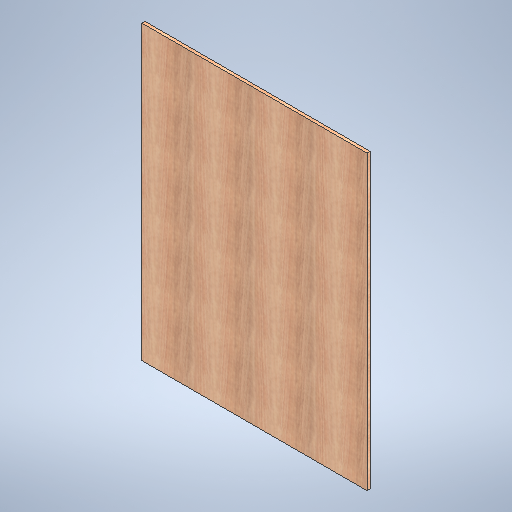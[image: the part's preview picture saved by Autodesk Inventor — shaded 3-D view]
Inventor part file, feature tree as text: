
AUTODESK INVENTOR PART (.ipt)
format: ipt  version: 2025 (Build 290162010, 162A)  size: 392,192 bytes
history: native  units: in
note: dims shown in document units (in); Inventor stores cm internally (conversion verified against a paired STEP export)
features: extrude x1, sketch x1
ambient origin geometry x8: Origin, YZ Plane, XZ Plane, XY Plane, X Axis, Y Axis, Z Axis, Center Point
bodies: Solid1 (feature_tree)
feature tree (2):
  extrude  "Extrusion1"  Depth=37.0in
  sketch  "Sketch1"  dims[d2=48.0in d3=37.0in d4=0.5in d5=0.0in]
